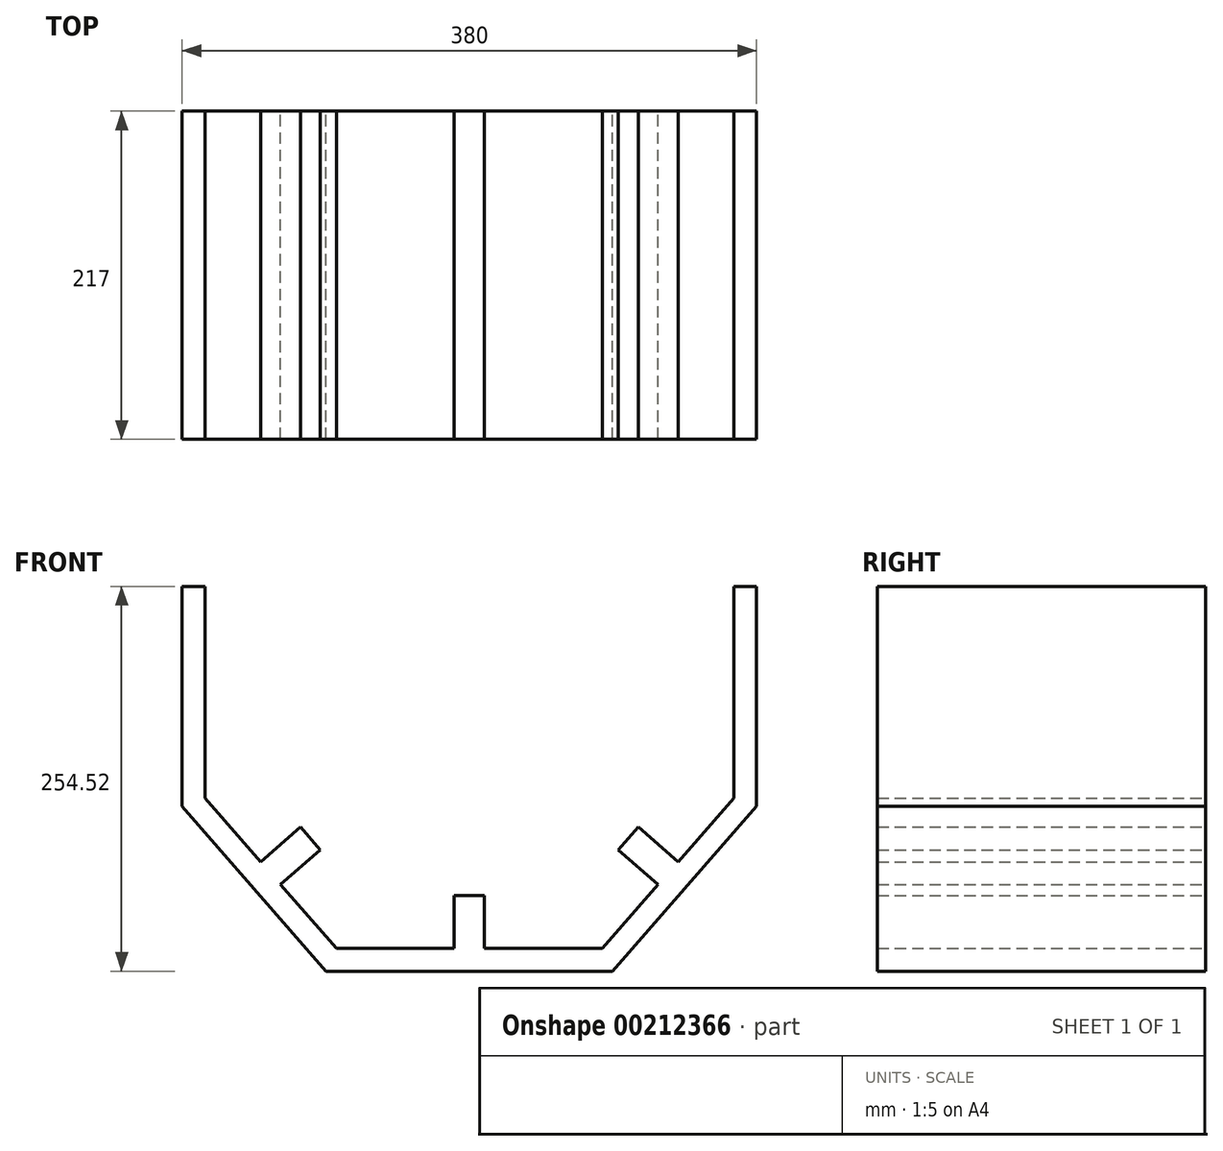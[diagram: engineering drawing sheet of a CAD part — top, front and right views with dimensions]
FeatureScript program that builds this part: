
annotation { "Feature Type Name" : "Feature", "Feature Type Description" : "" }
export const myFeature = defineFeature(function(context is Context, id is Id, definition is map)
    precondition{}
    {
        {
            var Q0;
            Q0=qCreatedBy(makeId("Front.planeOp"),FACE);
            var sketch = newSketch(context, id + "F0", { "sketchPlane" : qUnion([Q0])});
            skLineSegment(sketch, "E0", {"start": v(-190, 127.26) * mm, "end": v(-190, -18.26) * mm});
            skLineSegment(sketch, "E1", {"start": v(-175, 127.26) * mm, "end": v(-175, -12.63) * mm});
            skLineSegment(sketch, "E2", {"start": v(-190, -18.26) * mm, "end": v(-94.8, -127.26) * mm});
            skLineSegment(sketch, "E3", {"start": v(0, -127.26) * mm, "end": v(-94.8, -127.26) * mm});
            skLineSegment(sketch, "E4", {"start": v(190, -18.26) * mm, "end": v(94.8, -127.26) * mm});
            skLineSegment(sketch, "E5", {"start": v(0, -127.26) * mm, "end": v(94.8, -127.26) * mm});
            skLineSegment(sketch, "E6", {"start": v(-175, -12.63) * mm, "end": v(-138.07, -54.91) * mm});
            skLineSegment(sketch, "E7", {"start": v(-10, -112.26) * mm, "end": v(-87.98, -112.26) * mm});
            skLineSegment(sketch, "E8", {"start": v(10, -112.26) * mm, "end": v(87.98, -112.26) * mm});
            skLineSegment(sketch, "E9", {"start": v(175, -12.63) * mm, "end": v(138.07, -54.91) * mm});
            skLineSegment(sketch, "E10", {"start": v(-10, -77.26) * mm, "end": v(10, -77.26) * mm});
            skLineSegment(sketch, "E11", {"start": v(10, -112.26) * mm, "end": v(10, -77.26) * mm});
            skLineSegment(sketch, "E12", {"start": v(-10, -112.26) * mm, "end": v(-10, -77.26) * mm});
            skLineSegment(sketch, "E13", {"start": v(-111.7, -31.9) * mm, "end": v(-98.55, -46.95) * mm});
            skLineSegment(sketch, "E14", {"start": v(-138.07, -54.91) * mm, "end": v(-111.7, -31.9) * mm});
            skLineSegment(sketch, "E15", {"start": v(-124.91, -69.98) * mm, "end": v(-98.55, -46.95) * mm});
            skLineSegment(sketch, "E16", {"start": v(138.07, -54.91) * mm, "end": v(111.7, -31.9) * mm});
            skLineSegment(sketch, "E17", {"start": v(111.7, -31.9) * mm, "end": v(98.55, -46.95) * mm});
            skLineSegment(sketch, "E18", {"start": v(124.91, -69.98) * mm, "end": v(98.55, -46.95) * mm});
            skLineSegment(sketch, "E19", {"start": v(175, 127.26) * mm, "end": v(175, -12.63) * mm});
            skLineSegment(sketch, "E20", {"start": v(190, 127.26) * mm, "end": v(190, -18.26) * mm});
            skLineSegment(sketch, "E21", {"start": v(-190, 127.26) * mm, "end": v(-175, 127.26) * mm});
            skLineSegment(sketch, "E22", {"start": v(175, 127.26) * mm, "end": v(190, 127.26) * mm});
            skLineSegment(sketch, "E23.trimOffspring", {"start": v(-124.91, -69.98) * mm, "end": v(-87.98, -112.26) * mm});
            skLineSegment(sketch, "E24.trimOffspring", {"start": v(124.91, -69.98) * mm, "end": v(87.98, -112.26) * mm});
            skSolve(sketch);
        }
        {
            var Q0;
            Q0=makeQuery(id+"F0.imprint","IMPRINT",FACE,{"disambiguationData":[TD([[makeQuery(id+"F0.imprint","IMPRINT",EDGE,{"derivedFrom":sQuery(id+"F0.wireOp",EDGE,"E0")}),1.0]])]});
            extrude(context, id + "F1", {"entities" : qUnion([Q0]), "depth" : 217 * mm});
        }
    });
